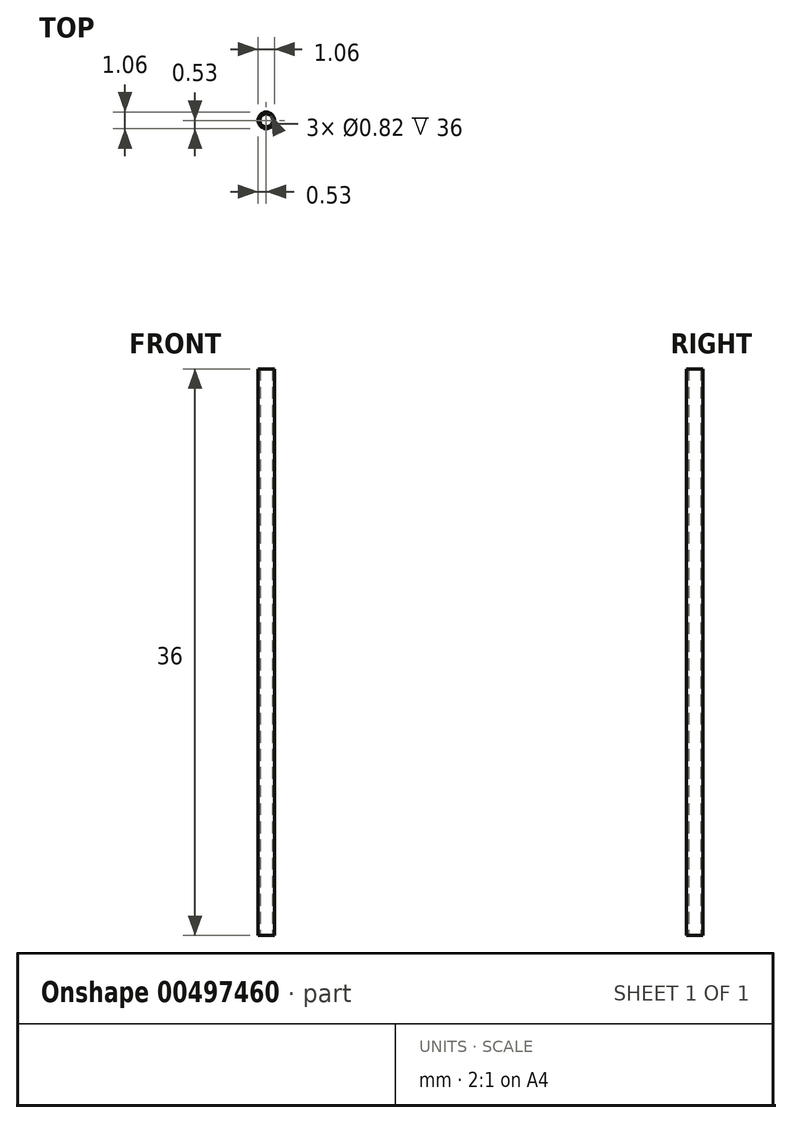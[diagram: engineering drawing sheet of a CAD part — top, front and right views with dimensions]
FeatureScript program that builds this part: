
annotation { "Feature Type Name" : "Feature", "Feature Type Description" : "" }
export const myFeature = defineFeature(function(context is Context, id is Id, definition is map)
    precondition{}
    {
        {
            var Q0;
            Q0=qCreatedBy(makeId("Top.planeOp"),FACE);
            var sketch = newSketch(context, id + "F0", { "sketchPlane" : qUnion([Q0])});
            skCircle(sketch, "E0", {"center": v(0, 0) * mm, "radius": 0.41 * mm});
            skCircle(sketch, "E1", {"center": v(0, 0) * mm, "radius": 0.53 * mm});
            skSolve(sketch);
        }
        {
            var Q0;
            Q0=makeQuery(id+"F0.imprint","IMPRINT",FACE,{"disambiguationData":[TD([[makeQuery(id+"F0.imprint","IMPRINT",EDGE,{"derivedFrom":sQuery(id+"F0.wireOp",EDGE,"E0")}),-1.0]])]});
            extrude(context, id + "F1", {"entities" : qUnion([Q0]), "depth" : 36 * mm});
        }
    });
